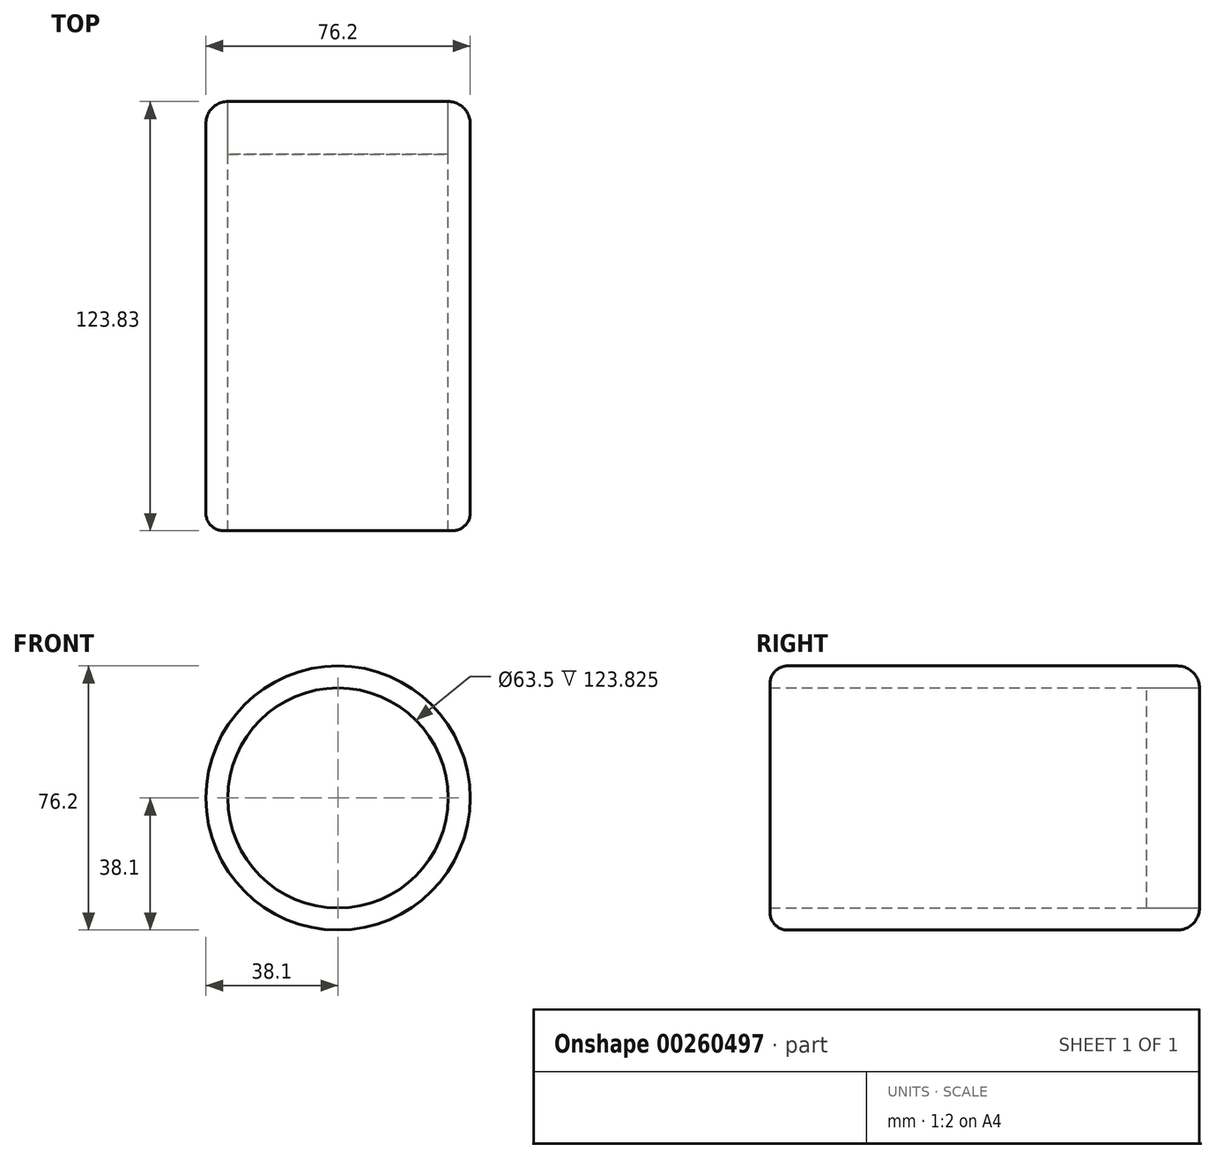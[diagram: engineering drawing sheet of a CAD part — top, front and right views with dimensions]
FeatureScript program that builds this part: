
annotation { "Feature Type Name" : "Feature", "Feature Type Description" : "" }
export const myFeature = defineFeature(function(context is Context, id is Id, definition is map)
    precondition{}
    {
        {
            var Q0;
            Q0=qCreatedBy(makeId("Front.planeOp"),FACE);
            var sketch = newSketch(context, id + "F0", { "sketchPlane" : qUnion([Q0])});
            skCircle(sketch, "E0", {"center": v(0, 0) * mm, "radius": 38.1 * mm});
            skCircle(sketch, "E1", {"center": v(0, 0) * mm, "radius": 31.75 * mm});
            skSolve(sketch);
        }
        {
            var Q0;
            Q0=makeQuery(id+"F0.imprint","IMPRINT",FACE,{"disambiguationData":[TD([[makeQuery(id+"F0.imprint","IMPRINT",EDGE,{"derivedFrom":sQuery(id+"F0.wireOp",EDGE,"E0")}),1.0]])]});
            extrude(context, id + "F1", {"entities" : qUnion([Q0]), "depth" : 123.82 * mm});
        }
        {
            var Q0;
            Q0=makeQuery(id+"F0.imprint","IMPRINT",FACE,{"disambiguationData":[TD([[makeQuery(id+"F0.imprint","IMPRINT",EDGE,{"derivedFrom":sQuery(id+"F0.wireOp",EDGE,"E1")}),1.0]])]});
            extrude(context, id + "F2", {"entities" : qUnion([Q0]), "depth" : 15.24 * mm});
        }
        {
            var Q0;
            Q0=makeQuery(id+"F1.opExtrude","CAP_EDGE",EDGE,{"disambiguationData":[OSD([sQuery(id+"F0.wireOp",EDGE,"E0")])],"isStart":true});
            fillet(context, id + "F3", {"entities" : qUnion([Q0]), "radius" : 6.35 * mm, "tangentPropagation" : true, "allowEdgeOverflow" : false});
        }
        {
            var Q0;
            Q0=makeQuery(id+"F1.opExtrude","CAP_EDGE",EDGE,{"disambiguationData":[OSD([sQuery(id+"F0.wireOp",EDGE,"E0")])],"isStart":false});
            fillet(context, id + "F4", {"entities" : qUnion([Q0]), "radius" : 5.08 * mm, "tangentPropagation" : true, "allowEdgeOverflow" : false});
        }
    });
